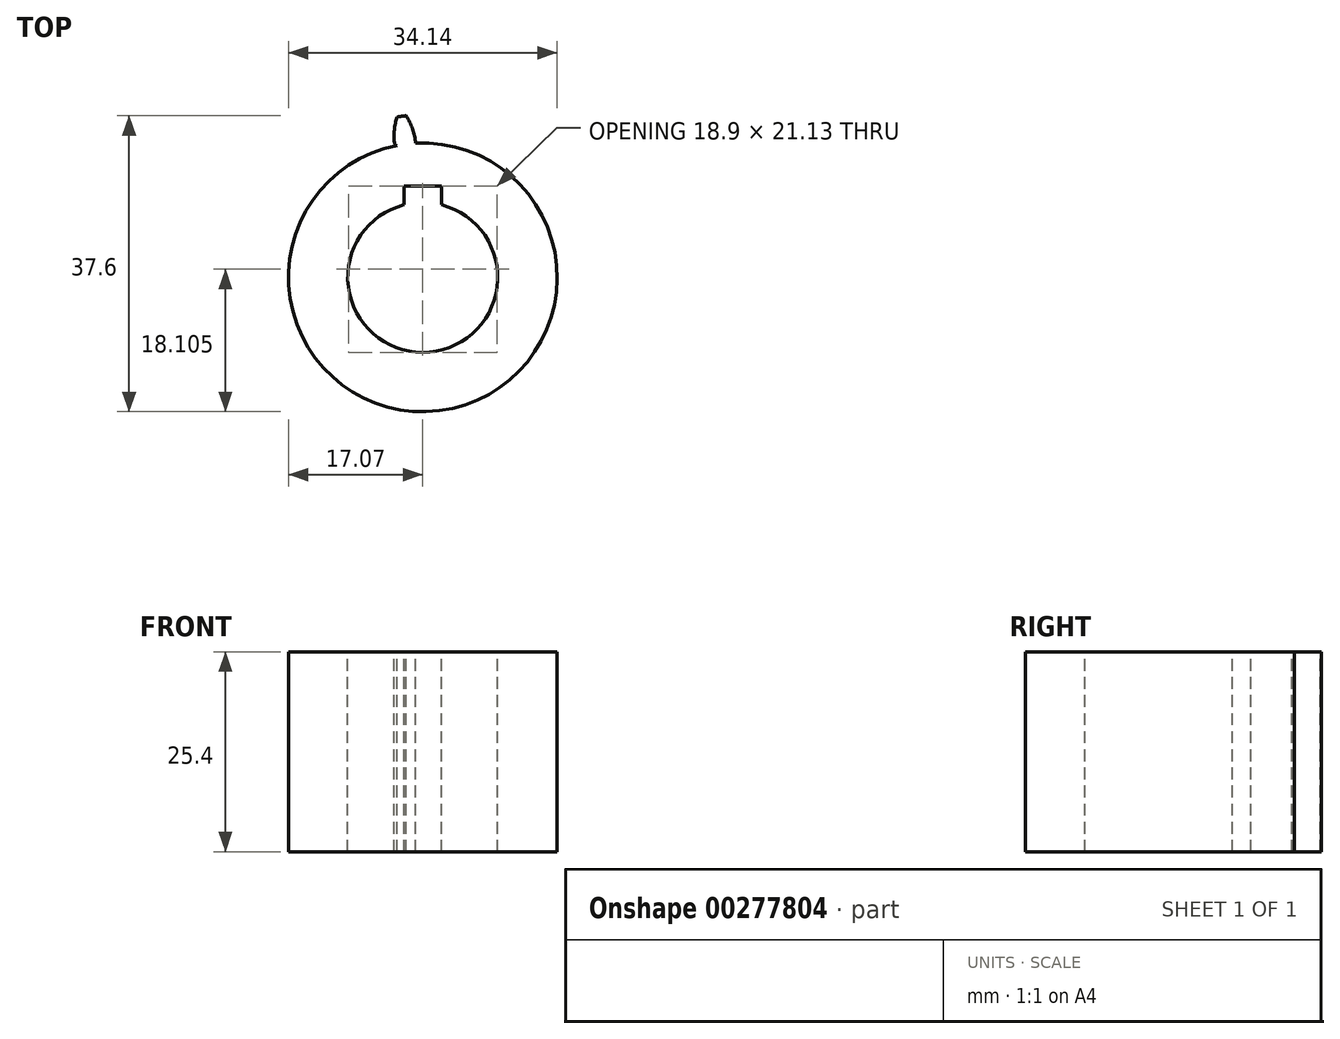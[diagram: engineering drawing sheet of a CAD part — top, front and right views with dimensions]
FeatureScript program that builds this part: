
annotation { "Feature Type Name" : "Feature", "Feature Type Description" : "" }
export const myFeature = defineFeature(function(context is Context, id is Id, definition is map)
    precondition{}
    {
        {
            var Q0;
            Q0=qCreatedBy(makeId("Top.planeOp"),FACE);
            var sketch = newSketch(context, id + "F0", { "sketchPlane" : qUnion([Q0])});
            skCircle(sketch, "E0", {"center": v(0, 0) * mm, "radius": 17.07 * mm});
            skSolve(sketch);
        }
        {
            var Q0;
            Q0=makeQuery(id+"F0.imprint","IMPRINT",FACE,{"disambiguationData":[TD([[makeQuery(id+"F0.imprint","IMPRINT",EDGE,{"derivedFrom":sQuery(id+"F0.wireOp",EDGE,"E0")}),1.0]])]});
            extrude(context, id + "F1", {"entities" : qUnion([Q0]), "depth" : 25.4 * mm});
        }
        {
            var Q0;
            Q0=makeQuery(id+"F1.opExtrude","CAP_FACE",FACE,{"disambiguationData":[OSD([sQuery(id+"F0.wireOp",EDGE,"E0")])],"isStart":false});
            var sketch = newSketch(context, id + "F2", { "sketchPlane" : qUnion([Q0])});
            skCircle(sketch, "E1.0", {"center": v(0, 0) * mm, "radius": 17.07 * mm, "construction": true});
            skArc(sketch, "E2", {"start": v(-2.38, 9.22) * mm, "mid": v(0, -9.53) * mm, "end": v(2.38, 9.22) * mm});
            skLineSegment(sketch, "E3", {"start": v(0, 17.07) * mm, "end": v(0, -17.07) * mm, "construction": true});
            skLineSegment(sketch, "E4", {"start": v(-2.38, 9.22) * mm, "end": v(-2.38, 11.6) * mm});
            skLineSegment(sketch, "E5", {"start": v(-2.38, 11.6) * mm, "end": v(2.38, 11.6) * mm});
            skLineSegment(sketch, "E6", {"start": v(2.38, 11.6) * mm, "end": v(2.38, 9.22) * mm});
            skSolve(sketch);
        }
        {
            var Q0;
            Q0 = qSketchRegion(id + "F2", true);
            extrude(context, id + "F3", {"entities" : qUnion([Q0]), "operationType" : NewBodyOperationType.REMOVE, "endBound" : BoundingType.THROUGH_ALL, "oppositeDirection" : true, "depth" : 25.4 * mm});
        }
        {
            var Q0;
            Q0=makeQuery(id+"F1.opExtrude","CAP_FACE",FACE,{"disambiguationData":[OSD([sQuery(id+"F0.wireOp",EDGE,"E0")])],"isStart":false});
            var sketch = newSketch(context, id + "F4", { "sketchPlane" : qUnion([Q0])});
            skLineSegment(sketch, "E7", {"start": v(0, 0) * mm, "end": v(0, 30.83) * mm, "construction": true});
            skLineSegment(sketch, "E8", {"start": v(0, 0) * mm, "end": v(-4.12, 31.27) * mm, "construction": true});
            skArc(sketch, "E9.0", {"start": v(-0.9, 17.04) * mm, "mid": v(-2.23, 16.92) * mm, "end": v(-3.54, 16.7) * mm});
            skArc(sketch, "E10", {"start": v(-2.11, 20.53) * mm, "mid": v(-2.4, 20.5) * mm, "end": v(-2.7, 20.46) * mm});
            skArc(sketch, "E11.trimOffspring", {"start": v(-0.9, 17.04) * mm, "mid": v(-1.3, 18.86) * mm, "end": v(-2.11, 20.53) * mm});
            skArc(sketch, "E12.MirrorCS", {"start": v(-3.27, 20.38) * mm, "mid": v(-2.98, 20.42) * mm, "end": v(-2.7, 20.46) * mm});
            skArc(sketch, "E13.MirrorCS", {"start": v(-3.54, 16.7) * mm, "mid": v(-3.63, 18.55) * mm, "end": v(-3.27, 20.38) * mm});
            skSolve(sketch);
        }
        {
            var Q0;
            Q0 = qSketchRegion(id + "F4", true);
            var Q1;
            Q1=makeQuery(id+"F1.opExtrude","CAP_FACE",FACE,{"disambiguationData":[OSD([sQuery(id+"F0.wireOp",EDGE,"E0")])],"isStart":true});
            extrude(context, id + "F5", {"entities" : qUnion([Q0]), "operationType" : NewBodyOperationType.ADD, "endBound" : BoundingType.UP_TO_SURFACE, "oppositeDirection" : true, "endBoundEntityFace" : qUnion([Q1]), "depth" : 25.4 * mm});
        }
        {
            var Q0;
            Q0=makeQuery(id+"F5.opExtrude","SWEPT_EDGE",EDGE,{"disambiguationData":[OSD([sQuery(id+"F0.wireOp",EDGE,"E0"),sQuery(id+"F4.wireOp",EDGE,"E9.0"),sQuery(id+"F4.wireOp",EDGE,"E11.trimOffspring")])]});
            var Q1;
            Q1=makeQuery(id+"F5.opExtrude","SWEPT_EDGE",EDGE,{"disambiguationData":[OSD([sQuery(id+"F0.wireOp",EDGE,"E0"),sQuery(id+"F4.wireOp",EDGE,"E9.0"),sQuery(id+"F4.wireOp",EDGE,"E13.MirrorCS")])]});
            fillet(context, id + "F6", {"entities" : qUnion([Q0, Q1]), "radius" : 0.4 * mm, "tangentPropagation" : true, "allowEdgeOverflow" : false});
        }
    });
